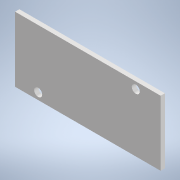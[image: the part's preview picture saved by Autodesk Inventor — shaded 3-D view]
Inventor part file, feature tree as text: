
AUTODESK INVENTOR PART (.ipt)
format: ipt  version: 2022 (Build 260153070, 153G)  size: 98,304 bytes
history: native  units: mm
features: extrude x1, sketch x1
ambient origin geometry x8: Origin, YZ Plane, XZ Plane, XY Plane, X Axis, Y Axis, Z Axis, Center Point
bodies: Solid1 (feature_tree)
feature tree (2):
  extrude  "Extrusion1"  Depth=24.2mm
  sketch  "Sketch1"  dims[d0=54.2mm d1=24.2mm d2=3.0mm d3=2.5mm d4=9.25mm d5=2.5mm d6=8.6mm d7=1.6mm d8=0.0mm]
